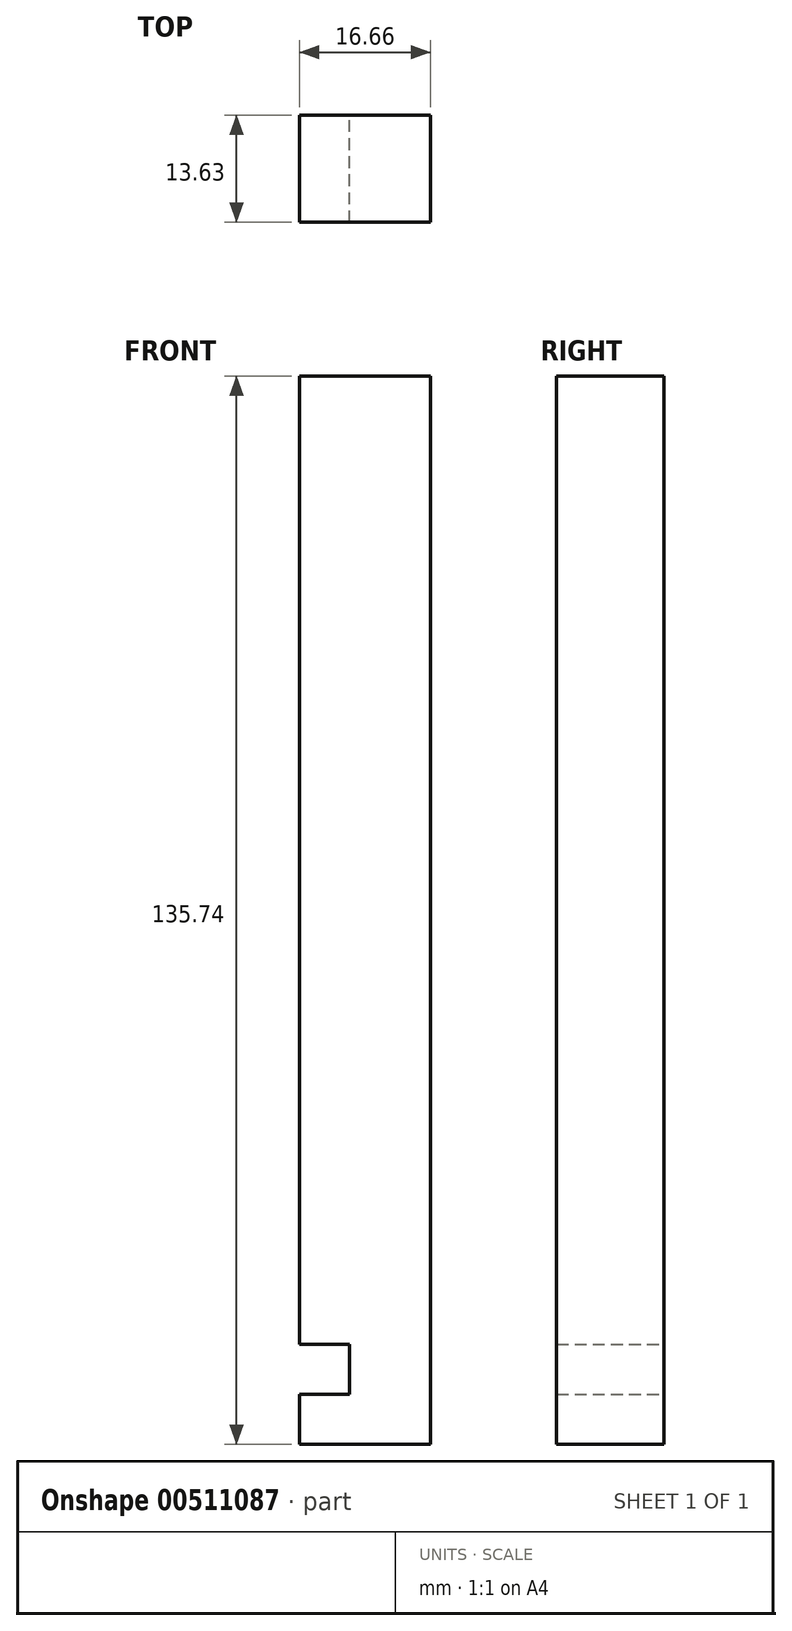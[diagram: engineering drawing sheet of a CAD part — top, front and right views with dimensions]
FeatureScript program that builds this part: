
annotation { "Feature Type Name" : "Feature", "Feature Type Description" : "" }
export const myFeature = defineFeature(function(context is Context, id is Id, definition is map)
    precondition{}
    {
        {
            assignVariable(context, id + "F0", {"name" : "thickness", "anyValue" : 0.66});
        }
        {
            assignVariable(context, id + "F1", {"name" : "bodyWidth", "anyValue" : 17.25});
        }
        {
            assignVariable(context, id + "F2", {"name" : "slideWidth", "anyValue" : 0.5});
        }
        {
            var Q0;
            Q0=qCreatedBy(makeId("Front.planeOp"),FACE);
            var sketch = newSketch(context, id + "F3", { "sketchPlane" : qUnion([Q0])});
            skLineSegment(sketch, "E0", {"start": v(0, 0) * mm, "end": v(0, 135.74) * mm});
            skLineSegment(sketch, "E1", {"start": v(0, 135.74) * mm, "end": v(-16.66, 135.74) * mm});
            skLineSegment(sketch, "E2", {"start": v(-16.66, 135.74) * mm, "end": v(-16.66, 12.7) * mm});
            skLineSegment(sketch, "E3", {"start": v(-16.66, 12.7) * mm, "end": v(-10.31, 12.7) * mm});
            skLineSegment(sketch, "E4", {"start": v(-10.31, 12.7) * mm, "end": v(-10.31, 6.35) * mm});
            skLineSegment(sketch, "E5", {"start": v(-10.31, 6.35) * mm, "end": v(-16.66, 6.35) * mm});
            skLineSegment(sketch, "E6", {"start": v(-16.66, 6.35) * mm, "end": v(-16.66, 0) * mm});
            skLineSegment(sketch, "E7", {"start": v(-16.66, 0) * mm, "end": v(0, 0) * mm});
            skSolve(sketch);
        }
        {
            var Q0;
            Q0 = qSketchRegion(id + "F3", true);
            extrude(context, id + "F4", {"entities" : qUnion([Q0]), "depth" : (getVariable(context, 'bodyWidth') - (getVariable(context, 'thickness') * 2) - (getVariable(context, 'slideWidth') * 2) - (getVariable(context, 'thickness') * 2)) * mm, "offsetDistance" : 25.4 * mm});
        }
    });
